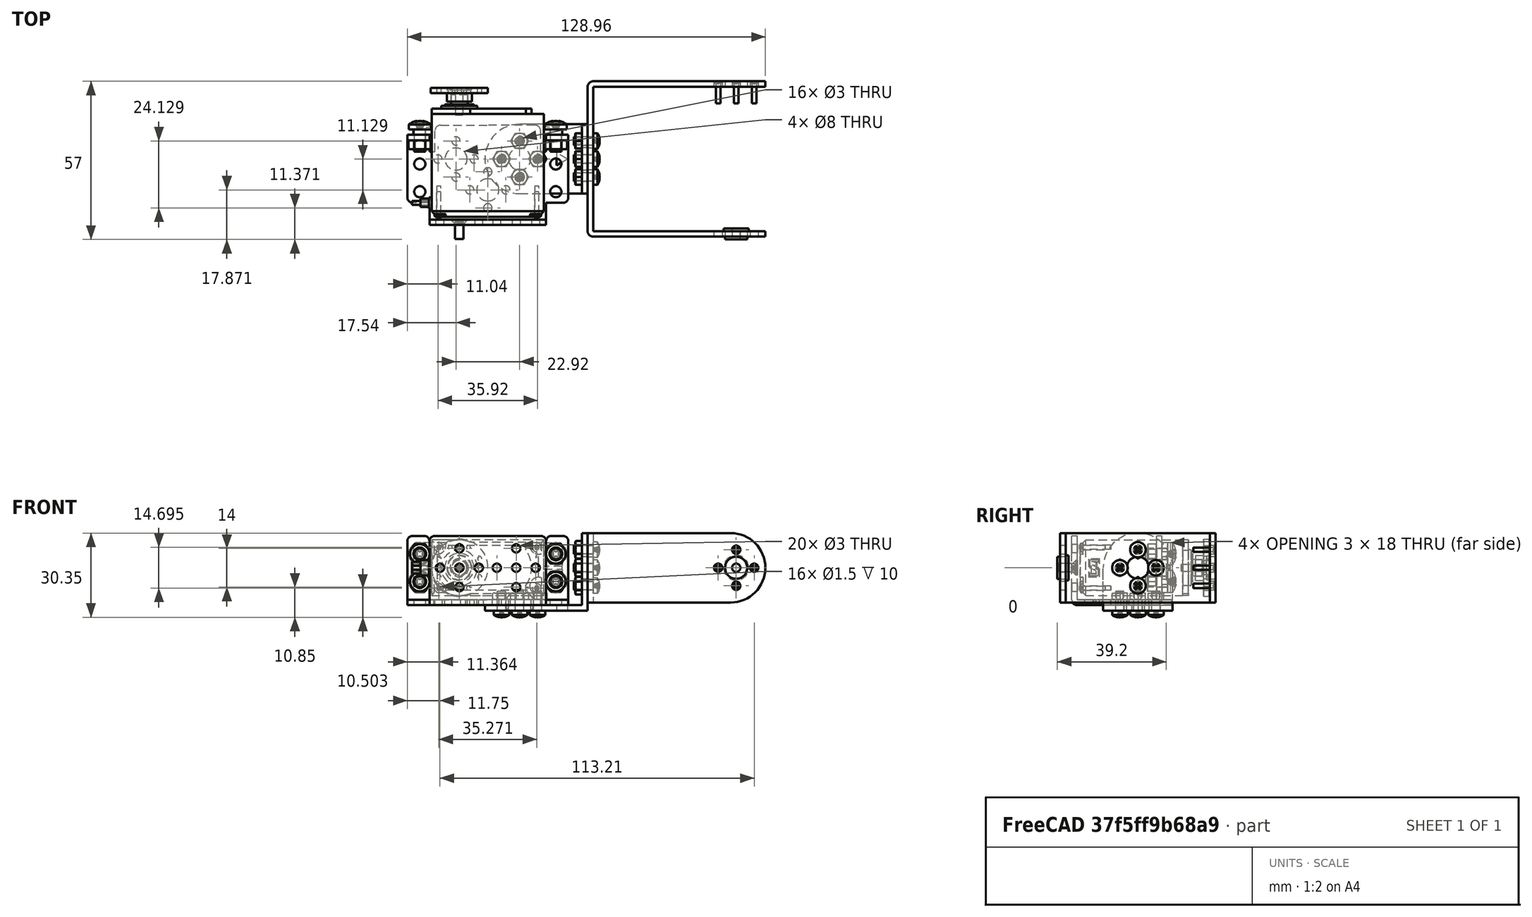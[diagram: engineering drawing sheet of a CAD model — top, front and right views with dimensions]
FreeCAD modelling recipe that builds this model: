
FCSTD DOCUMENT  (FreeCAD 0.19R24276 (Git))
Label: cuerpo_medio
License: All rights reserved
LicenseURL: http://en.wikipedia.org/wiki/All_rights_reserved
objects: Part::FeaturePython×35, App::FeaturePython×24, App::DocumentObjectGroup×5
note: 35 computed .brp shape members not serialized (recipe doc carries the construction recipe); baked Part::Feature solids carry a one-line shape summary decoded from their .brp

FEATURE [Part::FeaturePython] b_parte_servos_001_  label="parte_servos_001"  # a2plus imported part (geometry in sourceFile) (typed FeaturePython)
  a2p_Version = V0.1
  fixedPosition = true
  objectType = a2pPart
  sourceFile = .\..\piezas\parte_servos.FCStd
  subassemblyImport = false
  timeLastImport = 1.62041e+09
  updateColors = true
FEATURE [Part::FeaturePython] b_servo_001_  label="servo_001"  # a2plus imported part (geometry in sourceFile) (typed FeaturePython)
  Placement = pos=(4.5e-15,-15,13.5) rot=(-1,0,0;1.5708rad)
  a2p_Version = V0.1
  fixedPosition = false
  objectType = a2pPart
  sourceFile = .\..\piezas\servo.FCStd
  subassemblyImport = false
  timeLastImport = 1.62041e+09
  updateColors = true
FEATURE [Part::FeaturePython] b_parte_union_001_  label="parte_union_001"  # a2plus imported part (geometry in sourceFile) (typed FeaturePython)
  Placement = pos=(35.96,5.8,13.5) rot=(-0.57735,0.57735,-0.57735;2.0944rad)
  a2p_Version = V0.1
  fixedPosition = false
  objectType = a2pPart
  sourceFile = .\..\piezas\parte_union.FCStd
  subassemblyImport = false
  timeLastImport = 1.62041e+09
  updateColors = true
FEATURE [Part::FeaturePython] b_tapa_001_  label="tapa_001"  # a2plus imported part (geometry in sourceFile) (typed FeaturePython)
  Placement = pos=(-10.25,31.5,13.5) rot=(1,0,0;1.5708rad)
  a2p_Version = V0.1
  fixedPosition = false
  objectType = a2pPart
  sourceFile = .\..\piezas\tapa.FCStd
  subassemblyImport = false
  timeLastImport = 1.62021e+09
  updateColors = true
FEATURE [Part::FeaturePython] b_pieza_ultima_001_  label="pieza_ultima_001"  # a2plus imported part (geometry in sourceFile) (typed FeaturePython)
  Placement = pos=(35.96,5.8,-2) rot=(0,0,1;1.5708rad)
  a2p_Version = V0.1
  fixedPosition = false
  objectType = a2pPart
  sourceFile = .\..\piezas\pieza_ultima.FCStd
  subassemblyImport = false
  timeLastImport = 1.62041e+09
  updateColors = true
FEATURE [App::FeaturePython] planeCoincident_002  label="planeCoincident_002__servo_001"  # a2plus constraint (typed FeaturePython)
  Object1 = b_tapa_001_
  Object2 = b_servo_001_
  ParentTreeObject = -> b_tapa_001_
  SubElement1 = Face23
  SubElement2 = Face34
  Suppressed = false
  Type = plane
  directionConstraint = 1
  offset = 0
FEATURE [App::FeaturePython] planeCoincident_002_mirror  label="planeCoincident_002__tapa_001"  # a2plus constraint (typed FeaturePython)
  Object1 = b_tapa_001_
  Object2 = b_servo_001_
  ParentTreeObject = -> b_servo_001_
  SubElement1 = Face23
  SubElement2 = Face34
  Suppressed = false
  Type = plane
  directionConstraint = 1
  offset = 0
FEATURE [App::FeaturePython] axisCoincident_003  label="axisCoincident_003__servo_001"  # a2plus constraint (typed FeaturePython)
  Object1 = b_tapa_001_
  Object2 = b_servo_001_
  ParentTreeObject = -> b_tapa_001_
  SubElement1 = Face21
  SubElement2 = Face30
  Suppressed = false
  Type = axial
  directionConstraint = 1
  lockRotation = false
FEATURE [App::FeaturePython] axisCoincident_003_mirror  label="axisCoincident_003__tapa_001"  # a2plus constraint (typed FeaturePython)
  Object1 = b_tapa_001_
  Object2 = b_servo_001_
  ParentTreeObject = -> b_servo_001_
  SubElement1 = Face21
  SubElement2 = Face30
  Suppressed = false
  Type = axial
  directionConstraint = 1
  lockRotation = false
FEATURE [App::FeaturePython] axisCoincident_001  label="axisCoincident_001__parte_servos_001"  # a2plus constraint (typed FeaturePython)
  Object1 = b_servo_001_
  Object2 = b_parte_servos_001_
  ParentTreeObject = -> b_servo_001_
  SubElement1 = Face219
  SubElement2 = Face73
  Suppressed = false
  Type = axial
  directionConstraint = 0
  lockRotation = false
FEATURE [App::FeaturePython] axisCoincident_001_mirror  label="axisCoincident_001__servo_001"  # a2plus constraint (typed FeaturePython)
  Object1 = b_servo_001_
  Object2 = b_parte_servos_001_
  ParentTreeObject = -> b_parte_servos_001_
  SubElement1 = Face219
  SubElement2 = Face73
  Suppressed = false
  Type = axial
  directionConstraint = 0
  lockRotation = false
FEATURE [App::FeaturePython] axisCoincident_002  label="axisCoincident_002__parte_servos_001"  # a2plus constraint (typed FeaturePython)
  Object1 = b_servo_001_
  Object2 = b_parte_servos_001_
  ParentTreeObject = -> b_servo_001_
  SubElement1 = Face84
  SubElement2 = Face82
  Suppressed = false
  Type = axial
  directionConstraint = 0
  lockRotation = false
FEATURE [App::FeaturePython] axisCoincident_002_mirror  label="axisCoincident_002__servo_001"  # a2plus constraint (typed FeaturePython)
  Object1 = b_servo_001_
  Object2 = b_parte_servos_001_
  ParentTreeObject = -> b_parte_servos_001_
  SubElement1 = Face84
  SubElement2 = Face82
  Suppressed = false
  Type = axial
  directionConstraint = 0
  lockRotation = false
FEATURE [App::FeaturePython] axisCoincident_004  label="axisCoincident_004__parte_servos_001"  # a2plus constraint (typed FeaturePython)
  Object1 = b_pieza_ultima_001_
  Object2 = b_parte_servos_001_
  ParentTreeObject = -> b_pieza_ultima_001_
  SubElement1 = Face15
  SubElement2 = Face62
  Suppressed = false
  Type = axial
  directionConstraint = 0
  lockRotation = false
FEATURE [App::FeaturePython] axisCoincident_004_mirror  label="axisCoincident_004__pieza_ultima_001"  # a2plus constraint (typed FeaturePython)
  Object1 = b_pieza_ultima_001_
  Object2 = b_parte_servos_001_
  ParentTreeObject = -> b_parte_servos_001_
  SubElement1 = Face15
  SubElement2 = Face62
  Suppressed = false
  Type = axial
  directionConstraint = 0
  lockRotation = false
FEATURE [App::FeaturePython] planeCoincident_001  label="planeCoincident_001__parte_servos_001"  # a2plus constraint (typed FeaturePython)
  Object1 = b_pieza_ultima_001_
  Object2 = b_parte_servos_001_
  ParentTreeObject = -> b_pieza_ultima_001_
  SubElement1 = Face7
  SubElement2 = Face26
  Suppressed = false
  Type = plane
  directionConstraint = 0
  offset = 0
FEATURE [App::FeaturePython] planeCoincident_001_mirror  label="planeCoincident_001__pieza_ultima_001"  # a2plus constraint (typed FeaturePython)
  Object1 = b_pieza_ultima_001_
  Object2 = b_parte_servos_001_
  ParentTreeObject = -> b_parte_servos_001_
  SubElement1 = Face7
  SubElement2 = Face26
  Suppressed = false
  Type = plane
  directionConstraint = 0
  offset = 0
FEATURE [App::FeaturePython] axisCoincident_005  label="axisCoincident_005__pieza_ultima_001"  # a2plus constraint (typed FeaturePython)
  Object1 = b_parte_servos_001_
  Object2 = b_pieza_ultima_001_
  ParentTreeObject = -> b_parte_servos_001_
  SubElement1 = Face63
  SubElement2 = Face16
  Suppressed = false
  Type = axial
  directionConstraint = 0
  lockRotation = false
FEATURE [App::FeaturePython] axisCoincident_005_mirror  label="axisCoincident_005__parte_servos_001"  # a2plus constraint (typed FeaturePython)
  Object1 = b_parte_servos_001_
  Object2 = b_pieza_ultima_001_
  ParentTreeObject = -> b_pieza_ultima_001_
  SubElement1 = Face63
  SubElement2 = Face16
  Suppressed = false
  Type = axial
  directionConstraint = 0
  lockRotation = false
FEATURE [App::FeaturePython] planeCoincident_003  label="planeCoincident_003__pieza_ultima_001"  # a2plus constraint (typed FeaturePython)
  Object1 = b_parte_union_001_
  Object2 = b_pieza_ultima_001_
  ParentTreeObject = -> b_parte_union_001_
  SubElement1 = Face5
  SubElement2 = Face5
  Suppressed = false
  Type = plane
  directionConstraint = 1
  offset = 0
FEATURE [App::FeaturePython] planeCoincident_003_mirror  label="planeCoincident_003__parte_union_001"  # a2plus constraint (typed FeaturePython)
  Object1 = b_parte_union_001_
  Object2 = b_pieza_ultima_001_
  ParentTreeObject = -> b_pieza_ultima_001_
  SubElement1 = Face5
  SubElement2 = Face5
  Suppressed = false
  Type = plane
  directionConstraint = 1
  offset = 0
FEATURE [App::FeaturePython] axisCoincident_006  label="axisCoincident_006__pieza_ultima_001"  # a2plus constraint (typed FeaturePython)
  Object1 = b_parte_union_001_
  Object2 = b_pieza_ultima_001_
  ParentTreeObject = -> b_parte_union_001_
  SubElement1 = Face16
  SubElement2 = Face22
  Suppressed = false
  Type = axial
  directionConstraint = 1
  lockRotation = false
FEATURE [App::FeaturePython] axisCoincident_006_mirror  label="axisCoincident_006__parte_union_001"  # a2plus constraint (typed FeaturePython)
  Object1 = b_parte_union_001_
  Object2 = b_pieza_ultima_001_
  ParentTreeObject = -> b_pieza_ultima_001_
  SubElement1 = Face16
  SubElement2 = Face22
  Suppressed = false
  Type = axial
  directionConstraint = 1
  lockRotation = false
FEATURE [App::FeaturePython] axisCoincident_007  label="axisCoincident_007__parte_union_001"  # a2plus constraint (typed FeaturePython)
  Object1 = b_pieza_ultima_001_
  Object2 = b_parte_union_001_
  ParentTreeObject = -> b_pieza_ultima_001_
  SubElement1 = Face23
  SubElement2 = Face15
  Suppressed = false
  Type = axial
  directionConstraint = 1
  lockRotation = false
FEATURE [App::FeaturePython] axisCoincident_007_mirror  label="axisCoincident_007__pieza_ultima_001"  # a2plus constraint (typed FeaturePython)
  Object1 = b_pieza_ultima_001_
  Object2 = b_parte_union_001_
  ParentTreeObject = -> b_parte_union_001_
  SubElement1 = Face23
  SubElement2 = Face15
  Suppressed = false
  Type = axial
  directionConstraint = 1
  lockRotation = false
FEATURE [Part::FeaturePython] b_arandela_001_  label="arandela_001"  # a2plus imported part (geometry in sourceFile) (typed FeaturePython)
  Placement = pos=(89.46,-19.2,13.5) rot=(1,0,0;1.5708rad)
  a2p_Version = V0.1
  fixedPosition = false
  objectType = a2pPart
  sourceFile = .\..\piezas\arandela.FCStd
  subassemblyImport = false
  timeLastImport = 1.62024e+09
  updateColors = true
FEATURE [App::FeaturePython] planeCoincident_004  label="planeCoincident_004__parte_union_001"  # a2plus constraint (typed FeaturePython)
  Object1 = b_arandela_001_
  Object2 = b_parte_union_001_
  ParentTreeObject = -> b_arandela_001_
  SubElement1 = Face3
  SubElement2 = Face19
  Suppressed = false
  Type = plane
  directionConstraint = 0
  offset = 0
FEATURE [App::FeaturePython] planeCoincident_004_mirror  label="planeCoincident_004__arandela_001"  # a2plus constraint (typed FeaturePython)
  Object1 = b_arandela_001_
  Object2 = b_parte_union_001_
  ParentTreeObject = -> b_parte_union_001_
  SubElement1 = Face3
  SubElement2 = Face19
  Suppressed = false
  Type = plane
  directionConstraint = 0
  offset = 0
FEATURE [App::FeaturePython] axisCoincident_008  label="axisCoincident_008__parte_union_001"  # a2plus constraint (typed FeaturePython)
  Object1 = b_arandela_001_
  Object2 = b_parte_union_001_
  ParentTreeObject = -> b_arandela_001_
  SubElement1 = Face5
  SubElement2 = Face35
  Suppressed = false
  Type = axial
  directionConstraint = 1
  lockRotation = false
FEATURE [App::FeaturePython] axisCoincident_008_mirror  label="axisCoincident_008__arandela_001"  # a2plus constraint (typed FeaturePython)
  Object1 = b_arandela_001_
  Object2 = b_parte_union_001_
  ParentTreeObject = -> b_parte_union_001_
  SubElement1 = Face5
  SubElement2 = Face35
  Suppressed = false
  Type = axial
  directionConstraint = 1
  lockRotation = false
FEATURE [Part::FeaturePython] Screw  label="M3x7-Screw"  # Fasteners workbench fastener (typed FeaturePython)
  Placement = pos=(-10.25,-16,13.5) rot=(-1,0,0;1.5708rad)
  baseObject = -> b_parte_servos_001_ [Edge75]
  diameter = 4
  invert = false
  length = 11
  lengthCustom = 7
  matchOuter = false
  offset = 0
  thread = false
  type = 35
FEATURE [Part::FeaturePython] Screw005  label="M3x7-Screw001"  # Fasteners workbench fastener (typed FeaturePython)
  Placement = pos=(4.96,5.8,-2) rot=(-1,0,0;3.14159rad)
  baseObject = -> b_pieza_ultima_001_ [Edge21]
  diameter = 4
  invert = true
  length = 11
  lengthCustom = 7
  matchOuter = true
  offset = 0
  thread = false
  type = 34
FEATURE [Part::FeaturePython] Screw006  label="M3x7-Screw002"  # Fasteners workbench fastener (typed FeaturePython)
  Placement = pos=(11.46,12.3,-2) rot=(-1,0,0;3.14159rad)
  baseObject = -> b_pieza_ultima_001_ [Edge20]
  diameter = 4
  invert = true
  length = 11
  lengthCustom = 7
  matchOuter = true
  offset = 0
  thread = false
  type = 34
FEATURE [Part::FeaturePython] Screw007  label="M3x7-Screw003"  # Fasteners workbench fastener (typed FeaturePython)
  Placement = pos=(11.46,-0.7,-2) rot=(-1,0,0;3.14159rad)
  baseObject = -> b_pieza_ultima_001_ [Edge18]
  diameter = 4
  invert = true
  length = 11
  lengthCustom = 7
  matchOuter = true
  offset = 0
  thread = false
  type = 34
FEATURE [Part::FeaturePython] Screw008  label="M3x7-Screw004"  # Fasteners workbench fastener (typed FeaturePython)
  Placement = pos=(17.96,5.8,-2) rot=(-1,0,0;3.14159rad)
  baseObject = -> b_pieza_ultima_001_ [Edge17]
  diameter = 4
  invert = true
  length = 11
  lengthCustom = 7
  matchOuter = true
  offset = 0
  thread = false
  type = 34
FEATURE [Part::FeaturePython] Screw009  label="M3x7-Screw005"  # Fasteners workbench fastener (typed FeaturePython)
  Placement = pos=(37.96,12.3,13.5) rot=(0,1,0;1.5708rad)
  baseObject = -> b_parte_union_001_ [Edge30]
  diameter = 4
  invert = false
  length = 11
  lengthCustom = 7
  matchOuter = true
  offset = 0
  thread = false
  type = 34
FEATURE [Part::FeaturePython] Screw010  label="M3x7-Screw006"  # Fasteners workbench fastener (typed FeaturePython)
  Placement = pos=(37.96,5.8,7) rot=(0,1,0;1.5708rad)
  baseObject = -> b_parte_union_001_ [Edge31]
  diameter = 4
  invert = false
  length = 11
  lengthCustom = 7
  matchOuter = true
  offset = 0
  thread = false
  type = 34
FEATURE [Part::FeaturePython] Screw011  label="M3x7-Screw007"  # Fasteners workbench fastener (typed FeaturePython)
  Placement = pos=(37.96,-0.7,13.5) rot=(0,1,0;1.5708rad)
  baseObject = -> b_parte_union_001_ [Edge28]
  diameter = 4
  invert = false
  length = 11
  lengthCustom = 7
  matchOuter = true
  offset = 0
  thread = false
  type = 34
FEATURE [Part::FeaturePython] Screw012  label="M3x7-Screw008"  # Fasteners workbench fastener (typed FeaturePython)
  Placement = pos=(37.96,5.8,20) rot=(0,1,0;1.5708rad)
  baseObject = -> b_parte_union_001_ [Edge27]
  diameter = 4
  invert = false
  length = 11
  lengthCustom = 7
  matchOuter = true
  offset = 0
  thread = false
  type = 34
FEATURE [App::DocumentObjectGroup] Group002  label="ensamble"
  Group = -> [Screw005,Screw006,Screw007,Screw008,Screw009,Screw010,Screw011,Screw012]
FEATURE [Part::FeaturePython] Screw013  label="M4x8-Screw"  # Fasteners workbench fastener (typed FeaturePython)
  Placement = pos=(-24.5,16.5,8.5) rot=(-1,0,0;1.5708rad)
  baseObject = -> b_servo_001_ [Edge207]
  diameter = 6
  invert = true
  length = 12
  lengthCustom = 8
  matchOuter = true
  offset = 0
  thread = false
  type = 34
FEATURE [Part::FeaturePython] Screw014  label="M4x8-Screw001"  # Fasteners workbench fastener (typed FeaturePython)
  Placement = pos=(-24.5,16.5,18.5) rot=(-1,0,0;1.5708rad)
  baseObject = -> b_servo_001_ [Edge233]
  diameter = 6
  invert = true
  length = 12
  lengthCustom = 8
  matchOuter = true
  offset = 0
  thread = false
  type = 34
FEATURE [Part::FeaturePython] Screw015  label="M4x8-Screw002"  # Fasteners workbench fastener (typed FeaturePython)
  Placement = pos=(24.5,16.5,8.5) rot=(-1,0,0;1.5708rad)
  baseObject = -> b_servo_001_ [Edge677]
  diameter = 6
  invert = false
  length = 12
  lengthCustom = 8
  matchOuter = true
  offset = 0
  thread = false
  type = 34
FEATURE [Part::FeaturePython] Screw016  label="M4x8-Screw003"  # Fasteners workbench fastener (typed FeaturePython)
  Placement = pos=(24.5,16.5,18.5) rot=(-1,0,0;1.5708rad)
  baseObject = -> b_servo_001_ [Edge432]
  diameter = 6
  invert = false
  length = 12
  lengthCustom = 8
  matchOuter = true
  offset = 0
  thread = false
  type = 34
FEATURE [Part::FeaturePython] Nut  label="M3-Nut"  # Fasteners workbench fastener (typed FeaturePython)
  Placement = pos=(11.46,12.3,2) rot=(0,0,1;0rad)
  baseObject = -> b_parte_servos_001_ [Edge159]
  diameter = 4
  invert = false
  matchOuter = true
  offset = 0
  thread = false
  type = 7
FEATURE [Part::FeaturePython] Nut001  label="M3-Nut001"  # Fasteners workbench fastener (typed FeaturePython)
  Placement = pos=(4.96,5.8,2) rot=(0,0,1;0rad)
  baseObject = -> b_parte_servos_001_ [Edge157]
  diameter = 4
  invert = false
  matchOuter = true
  offset = 0
  thread = false
  type = 7
FEATURE [Part::FeaturePython] Nut003  label="M3-Nut003"  # Fasteners workbench fastener (typed FeaturePython)
  Placement = pos=(17.96,5.8,2) rot=(0,0,1;0rad)
  baseObject = -> b_parte_servos_001_ [Edge160]
  diameter = 4
  invert = false
  matchOuter = true
  offset = 0
  thread = false
  type = 7
FEATURE [Part::FeaturePython] Nut016  label="M3-Nut009"  # Fasteners workbench fastener (typed FeaturePython)
  Placement = pos=(33.96,12.3,13.5) rot=(0,-1,0;1.5708rad)
  baseObject = -> b_pieza_ultima_001_ [Edge56]
  diameter = 4
  invert = false
  matchOuter = true
  offset = 0
  thread = false
  type = 7
FEATURE [Part::FeaturePython] Nut017  label="M3-Nut010"  # Fasteners workbench fastener (typed FeaturePython)
  Placement = pos=(33.96,5.8,7) rot=(0,-1,0;1.5708rad)
  baseObject = -> b_pieza_ultima_001_ [Edge64]
  diameter = 4
  invert = false
  matchOuter = true
  offset = 0
  thread = false
  type = 7
FEATURE [Part::FeaturePython] Nut018  label="M3-Nut011"  # Fasteners workbench fastener (typed FeaturePython)
  Placement = pos=(33.96,5.8,20) rot=(0,-1,0;1.5708rad)
  baseObject = -> b_pieza_ultima_001_ [Edge58]
  diameter = 4
  invert = false
  matchOuter = true
  offset = 0
  thread = false
  type = 7
FEATURE [Part::FeaturePython] Nut019  label="M3-Nut012"  # Fasteners workbench fastener (typed FeaturePython)
  Placement = pos=(33.96,-0.7,13.5) rot=(0,-1,0;1.5708rad)
  baseObject = -> b_pieza_ultima_001_ [Edge62]
  diameter = 4
  invert = false
  matchOuter = true
  offset = 0
  thread = false
  type = 7
FEATURE [Part::FeaturePython] Nut020  label="M3-Nut013"  # Fasteners workbench fastener (typed FeaturePython)
  Placement = pos=(11.46,-0.7,2) rot=(0,0,1;0rad)
  baseObject = -> b_parte_servos_001_ [Edge155]
  diameter = 4
  invert = false
  matchOuter = false
  offset = 0
  thread = false
  type = 7
FEATURE [App::DocumentObjectGroup] Group003  label="ensamble001"
  Group = -> [Nut,Nut001,Nut003,Nut016,Nut017,Nut018,Nut019,Nut020]
FEATURE [Part::FeaturePython] Nut021  label="M4-Nut"  # Fasteners workbench fastener (typed FeaturePython)
  Placement = pos=(-24.5,12.5,18.5) rot=(1,0,0;1.5708rad)
  baseObject = -> b_parte_servos_001_ [Edge192]
  diameter = 6
  invert = true
  matchOuter = true
  offset = 0
  thread = false
  type = 7
FEATURE [Part::FeaturePython] Nut022  label="M4-Nut001"  # Fasteners workbench fastener (typed FeaturePython)
  Placement = pos=(-24.5,12.5,8.5) rot=(1,0,0;1.5708rad)
  baseObject = -> b_parte_servos_001_ [Edge193]
  diameter = 6
  invert = true
  matchOuter = true
  offset = 0
  thread = false
  type = 7
FEATURE [Part::FeaturePython] Nut023  label="M4-Nut002"  # Fasteners workbench fastener (typed FeaturePython)
  Placement = pos=(24.5,12.5,18.5) rot=(1,0,0;1.5708rad)
  baseObject = -> b_parte_servos_001_ [Edge219]
  diameter = 6
  invert = true
  matchOuter = true
  offset = 0
  thread = false
  type = 7
FEATURE [Part::FeaturePython] Nut024  label="M4-Nut003"  # Fasteners workbench fastener (typed FeaturePython)
  Placement = pos=(24.5,12.5,8.5) rot=(1,0,0;1.5708rad)
  baseObject = -> b_parte_servos_001_ [Edge220]
  diameter = 6
  invert = true
  matchOuter = true
  offset = 0
  thread = false
  type = 7
FEATURE [App::DocumentObjectGroup] Group001  label="tuercas"
  Group = -> [Group003,Nut021,Nut022,Nut023,Nut024]
FEATURE [Part::FeaturePython] Screw017  label="M1.6x8-Screw"  # Fasteners workbench fastener (typed FeaturePython)
  Placement = pos=(89.46,33.8,7) rot=(-1,0,0;1.5708rad)
  baseObject = -> b_parte_union_001_ [Edge45]
  diameter = 1
  invert = true
  length = 4
  lengthCustom = 8
  matchOuter = false
  offset = 0
  thread = false
  type = 35
FEATURE [Part::FeaturePython] Screw018  label="M1.6x8-Screw001"  # Fasteners workbench fastener (typed FeaturePython)
  Placement = pos=(82.96,33.8,13.5) rot=(-1,0,0;1.5708rad)
  baseObject = -> b_parte_union_001_ [Edge49]
  diameter = 1
  invert = true
  length = 4
  lengthCustom = 8
  matchOuter = false
  offset = 0
  thread = false
  type = 35
FEATURE [Part::FeaturePython] Screw019  label="M1.6x8-Screw002"  # Fasteners workbench fastener (typed FeaturePython)
  Placement = pos=(95.96,33.8,13.5) rot=(-1,0,0;1.5708rad)
  baseObject = -> b_parte_union_001_ [Edge46]
  diameter = 1
  invert = true
  length = 4
  lengthCustom = 8
  matchOuter = false
  offset = 0
  thread = false
  type = 35
FEATURE [Part::FeaturePython] Screw020  label="M1.6x8-Screw003"  # Fasteners workbench fastener (typed FeaturePython)
  Placement = pos=(89.46,33.8,20) rot=(-1,0,0;1.5708rad)
  baseObject = -> b_parte_union_001_ [Edge48]
  diameter = 1
  invert = true
  length = 4
  lengthCustom = 8
  matchOuter = false
  offset = 0
  thread = false
  type = 35
FEATURE [App::DocumentObjectGroup] Group004  label="acople"
  Group = -> [Screw017,Screw018,Screw019,Screw020]
FEATURE [App::DocumentObjectGroup] Group  label="tornillos"
  Group = -> [Screw,Group002,Screw013,Screw014,Screw015,Screw016,Group004]
